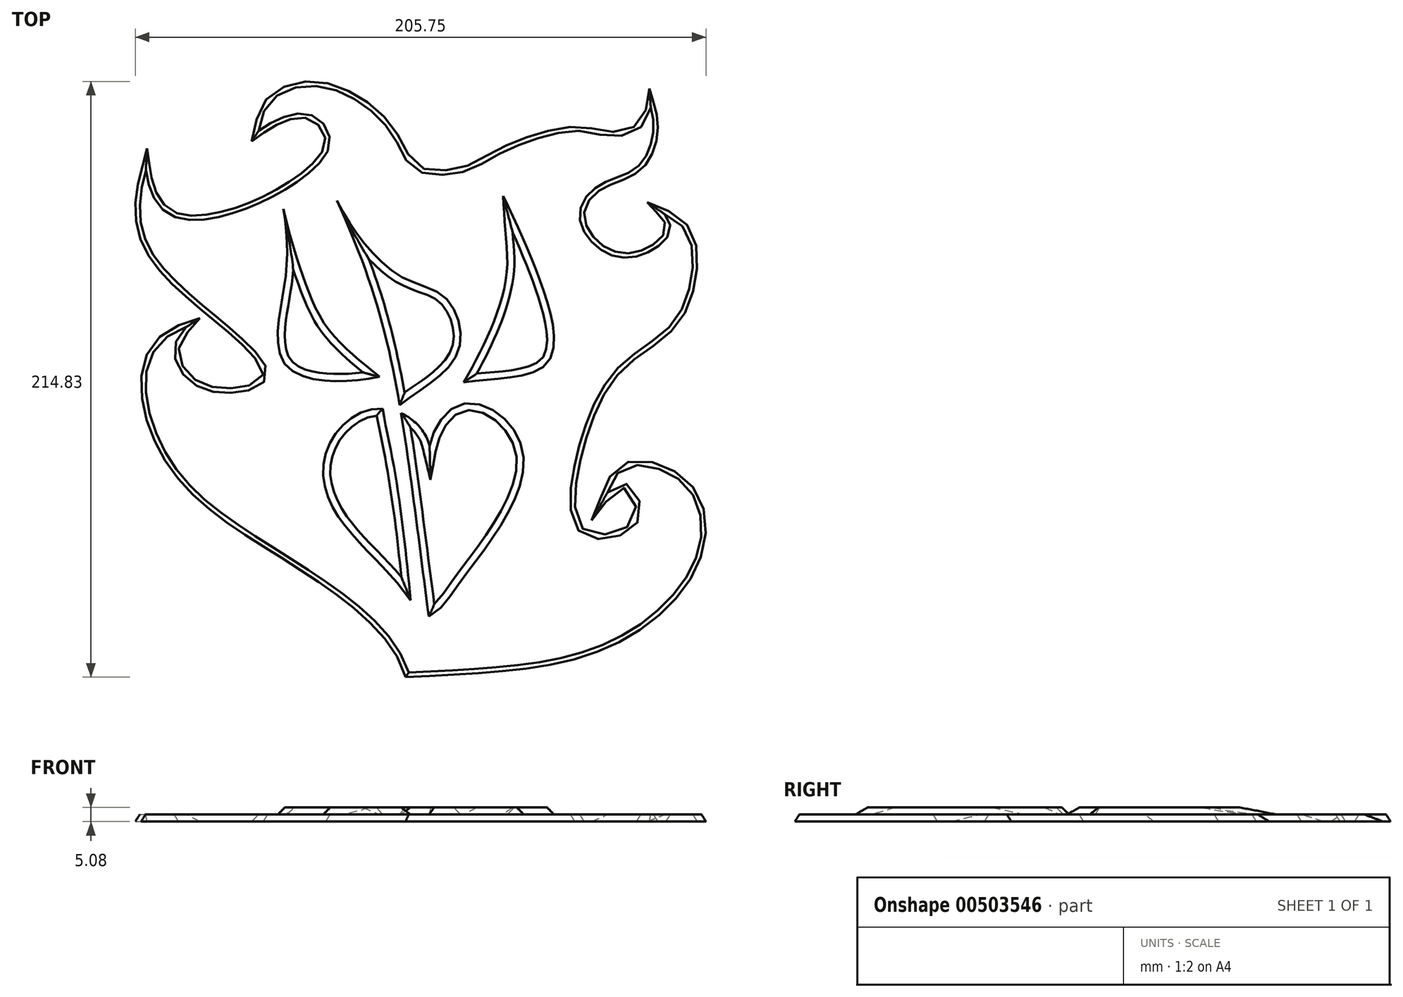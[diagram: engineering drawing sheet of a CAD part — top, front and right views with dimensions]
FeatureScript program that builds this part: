
annotation { "Feature Type Name" : "Feature", "Feature Type Description" : "" }
export const myFeature = defineFeature(function(context is Context, id is Id, definition is map)
    precondition{}
    {
        {
            var Q0;
            Q0=qCreatedBy(makeId("Top.planeOp"),FACE);
            var sketch = newSketch(context, id + "F0", { "sketchPlane" : qUnion([Q0])});
            skFitSpline(sketch, "E0", {"points": [v(-2.85, -60.94) * mm, v(-48.74, -17.72) * mm, v(-85.02, 10.3) * mm, v(-97.53, 39.01) * mm, v(-94.18, 55.9) * mm, v(-83.07, 63.63) * mm], "startDerivative": vector(-54.09, 184.74) * mm, "endDerivative": vector(100.5, 32.67) * mm});
            skFitSpline(sketch, "E1", {"points": [v(-83.07, 63.63) * mm, v(-87.45, 55.26) * mm, v(-76.81, 41.3) * mm, v(-53.8, 46.1) * mm, v(-91.3, 84.88) * mm, v(-97.63, 120.15) * mm], "startDerivative": vector(-54.41, -62.57) * mm, "endDerivative": vector(46.18, 175.7) * mm});
            skFitSpline(sketch, "E2", {"points": [v(-97.63, 120.15) * mm, v(-74.86, 102.72) * mm, v(-42.36, 116.53) * mm, v(-31.25, 131.2) * mm, v(-40.13, 140.68) * mm, v(-56.99, 134.38) * mm], "startDerivative": vector(33.56, -229.32) * mm, "endDerivative": vector(-59.82, -43.36) * mm});
            skFitSpline(sketch, "E3", {"points": [v(-56.99, 134.38) * mm, v(-53.38, 144.2) * mm, v(-34.76, 150.42) * mm, v(-9.59, 134.38) * mm, v(0, 120.15) * mm, v(18.44, 120.15) * mm, v(29.84, 126.2) * mm, v(57.27, 134.38) * mm, v(69.95, 132.43) * mm, v(84.41, 142.8) * mm], "startDerivative": vector(18.3, 83.24) * mm, "endDerivative": vector(39.02, 242.33) * mm});
            skFitSpline(sketch, "E4", {"points": [v(84.41, 142.8) * mm, v(80.65, 122.37) * mm, v(66.11, 114.96) * mm, v(58.87, 105.16) * mm, v(63.1, 94.38) * mm, v(76.87, 88.7) * mm, v(90.99, 97.37) * mm, v(89.44, 104.39) * mm], "startDerivative": vector(36.92, -115.54) * mm, "endDerivative": vector(-45.06, 46.04) * mm});
            skFitSpline(sketch, "E5", {"points": [v(89.44, 104.39) * mm, v(99.59, 87.7) * mm, v(92.79, 65.63) * mm, v(75.44, 51.62) * mm, v(61.2, 28.82) * mm, v(57.87, -9.19) * mm, v(73.07, -11.56) * mm, v(80.67, -3.96) * mm, v(76.87, 6.49) * mm, v(68.85, 3.98) * mm], "startDerivative": vector(222.8, -87.77) * mm, "endDerivative": vector(-106.95, -138) * mm});
            skFitSpline(sketch, "E6", {"points": [v(68.85, 3.98) * mm, v(75.23, 13.02) * mm, v(96.95, 6.6) * mm, v(100.62, -19.72) * mm, v(67.88, -50.62) * mm, v(-2.85, -60.94) * mm], "startDerivative": vector(30.9, 76.25) * mm, "endDerivative": vector(-279.6, -15.27) * mm});
            skSolve(sketch);
        }
        {
            var Q0;
            Q0 = qSketchRegion(id + "F0", true);
            extrude(context, id + "F1", {"entities" : qUnion([Q0]), "oppositeDirection" : true, "depth" : 2.54 * mm, "hasDraft" : true, "draftAngle" : 32 * degree});
        }
        {
            var Q0;
            Q0=qCreatedBy(makeId("Top.planeOp"),FACE);
            var sketch = newSketch(context, id + "F2", { "sketchPlane" : qUnion([Q0])});
            skFitSpline(sketch, "E7", {"points": [v(-2.24, -34.92) * mm, v(-28.12, -4.8) * mm, v(-32.53, 18.72) * mm, v(-14.8, 34.2) * mm, v(4.68, 20.71) * mm], "startDerivative": vector(-75.05, 112.43) * mm, "endDerivative": vector(26.98, -112.3) * mm});
            skFitSpline(sketch, "E8", {"points": [v(4.68, 20.71) * mm, v(17.34, 36.18) * mm, v(38.58, 17.05) * mm, v(15.72, -28.25) * mm, v(9.03, -37.3) * mm, v(4.39, -40.65) * mm], "startDerivative": vector(17.24, 91.78) * mm, "endDerivative": vector(-29.22, -14) * mm});
            skFitSpline(sketch, "E9", {"points": [v(4.39, -40.65) * mm, v(-11.04, 59.73) * mm, v(-29.73, 111.5) * mm], "startDerivative": vector(-27.66, 208.31) * mm, "endDerivative": vector(-53.04, 116.64) * mm});
            skFitSpline(sketch, "E10", {"points": [v(-29.73, 111.5) * mm, v(-6.56, 82.42) * mm, v(10.4, 74.13) * mm, v(14.67, 54.14) * mm, v(-6.1, 35.47) * mm], "startDerivative": vector(43.31, -102) * mm, "endDerivative": vector(-71.57, -59.26) * mm});
            skFitSpline(sketch, "E11", {"points": [v(17.03, 43.73) * mm, v(32.25, 95.61) * mm, v(31.23, 110.93) * mm], "startDerivative": vector(79.75, 140.4) * mm, "endDerivative": vector(-1.26, 33.71) * mm});
            skFitSpline(sketch, "E12", {"points": [v(31.23, 110.93) * mm, v(43.09, 84.11) * mm, v(47.45, 51.05) * mm, v(17.03, 43.73) * mm], "startDerivative": vector(35.77, -73.81) * mm, "endDerivative": vector(-101.23, -15.82) * mm});
            skFitSpline(sketch, "E13", {"points": [v(-13.37, 45.75) * mm, v(-37.84, 73.76) * mm, v(-47.99, 106.26) * mm], "startDerivative": vector(-96.08, 75.96) * mm, "endDerivative": vector(-12.48, 57.09) * mm});
            skFitSpline(sketch, "E14", {"points": [v(-47.99, 106.26) * mm, v(-47.99, 76.63) * mm, v(-47.05, 49.8) * mm, v(-13.37, 45.75) * mm], "startDerivative": vector(17.24, -112.36) * mm, "endDerivative": vector(103.37, 20.67) * mm});
            skFitSpline(sketch, "E15", {"points": [v(-2.24, -34.92) * mm, v(-7.99, 12.16) * mm, v(-12.28, 34.25) * mm], "startDerivative": vector(-6.62, 82.05) * mm, "endDerivative": vector(-8.19, 47.87) * mm});
            skFitSpline(sketch, "E16.trimOffspring", {"points": [v(4.39, -40.65) * mm, v(-11.04, 59.73) * mm, v(-29.73, 111.5) * mm], "startDerivative": vector(-27.66, 208.31) * mm, "endDerivative": vector(-53.04, 116.64) * mm});
            skSolve(sketch);
        }
        {
            var Q0;
            Q0=makeQuery(id+"F2.imprint","IMPRINT",FACE,{"disambiguationData":[TD([[makeQuery(id+"F2.imprint","IMPRINT",EDGE,{"derivedFrom":sQuery(id+"F2.wireOp",EDGE,"E8")}),-1.0]])]});
            var Q1;
            Q1=makeQuery(id+"F2.imprint","IMPRINT",FACE,{"disambiguationData":[TD([[makeQuery(id+"F2.imprint","IMPRINT",EDGE,{"derivedFrom":sQuery(id+"F2.wireOp",EDGE,"E7")}),-1.0]])]});
            var Q2;
            Q2=makeQuery(id+"F2.imprint","IMPRINT",FACE,{"disambiguationData":[TD([[makeQuery(id+"F2.imprint","IMPRINT",EDGE,{"derivedFrom":sQuery(id+"F2.wireOp",EDGE,"E13")}),1.0]])]});
            var Q3;
            {var subQ0=sQuery(id+"F2.wireOp",EDGE,"E16.trimOffspring");var subQ1=sQuery(id+"F2.wireOp",EDGE,"E10");var subQ2=makeQuery(id+"F2.imprint","INTERSECT",VERTEX,{"disambiguationData":[OD(1.0)],"derivedFrom":[subQ1,subQ0]});Q3=makeQuery(id+"F2.imprint","IMPRINT",FACE,{"disambiguationData":[TD([[makeQuery(id+"F2.imprint","IMPRINT",EDGE,{"disambiguationData":[TD([[subQ2,1.0]])],"derivedFrom":subQ1}),-1.0]])]});}
            var Q4;
            Q4=makeQuery(id+"F2.imprint","IMPRINT",FACE,{"disambiguationData":[TD([[makeQuery(id+"F2.imprint","IMPRINT",EDGE,{"derivedFrom":sQuery(id+"F2.wireOp",EDGE,"E11")}),-1.0]])]});
            extrude(context, id + "F3", {"entities" : qUnion([Q0, Q1, Q2, Q3, Q4]), "operationType" : NewBodyOperationType.ADD, "depth" : 2.54 * mm, "hasDraft" : true, "draftAngle" : 45 * degree, "draftPullDirection" : true});
        }
    });
